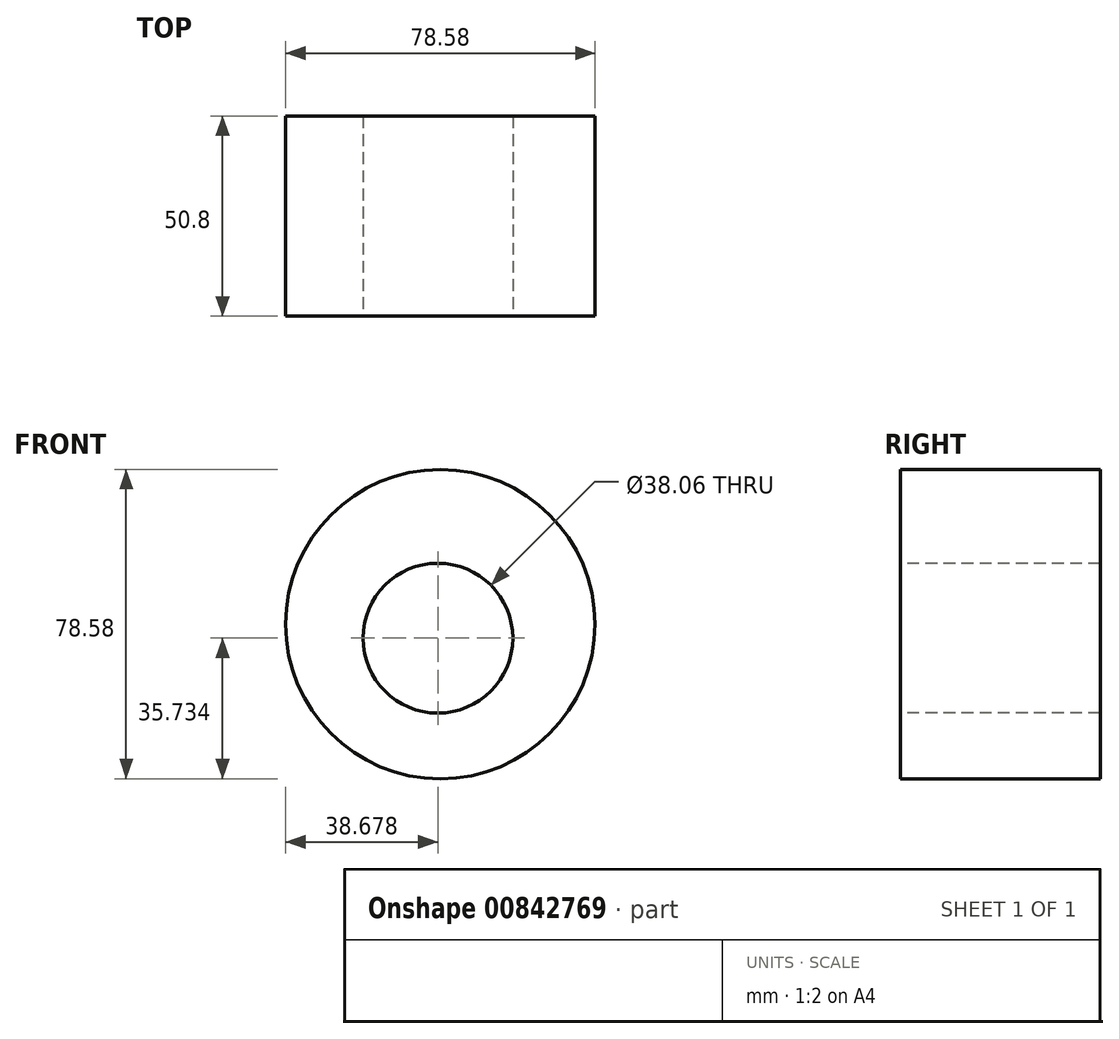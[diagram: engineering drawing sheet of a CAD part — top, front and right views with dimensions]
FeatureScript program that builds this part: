
annotation { "Feature Type Name" : "Feature", "Feature Type Description" : "" }
export const myFeature = defineFeature(function(context is Context, id is Id, definition is map)
    precondition{}
    {
        {
            var Q0;
            Q0=qCreatedBy(makeId("Front.planeOp"),FACE);
            var sketch = newSketch(context, id + "F0", { "sketchPlane" : qUnion([Q0])});
            skCircle(sketch, "E0", {"center": v(-10.6, 24.29) * mm, "radius": 39.29 * mm});
            skSolve(sketch);
        }
        {
            var Q0;
            Q0=makeQuery(id+"F0.imprint","IMPRINT",FACE,{"disambiguationData":[TD([[makeQuery(id+"F0.imprint","IMPRINT",EDGE,{"derivedFrom":sQuery(id+"F0.wireOp",EDGE,"E0")}),1.0]])]});
            extrude(context, id + "F1", {"entities" : qUnion([Q0]), "oppositeDirection" : true, "depth" : 50.8 * mm, "offsetDistance" : 25.4 * mm});
        }
        {
            var Q0;
            Q0=makeQuery(id+"F1.opExtrude","CAP_FACE",FACE,{"disambiguationData":[OSD([sQuery(id+"F0.wireOp",EDGE,"E0")])],"isStart":true});
            var sketch = newSketch(context, id + "F2", { "sketchPlane" : qUnion([Q0])});
            skCircle(sketch, "E1", {"center": v(-11.21, 20.73) * mm, "radius": 19.03 * mm});
            skSolve(sketch);
        }
        {
            var Q0;
            Q0 = qSketchRegion(id + "F2", true);
            extrude(context, id + "F3", {"entities" : qUnion([Q0]), "operationType" : NewBodyOperationType.REMOVE, "depth" : 25 * mm, "offsetDistance" : 25 * mm});
        }
        {
            var Q0;
            Q0=makeQuery(id+"F2.imprint","IMPRINT",FACE,{"disambiguationData":[TD([[makeQuery(id+"F2.imprint","IMPRINT",EDGE,{"derivedFrom":sQuery(id+"F2.wireOp",EDGE,"E1")}),1.0]])]});
            extrude(context, id + "F4", {"entities" : qUnion([Q0]), "operationType" : NewBodyOperationType.REMOVE, "oppositeDirection" : true, "depth" : 71 * mm, "offsetDistance" : 25 * mm});
        }
    });
